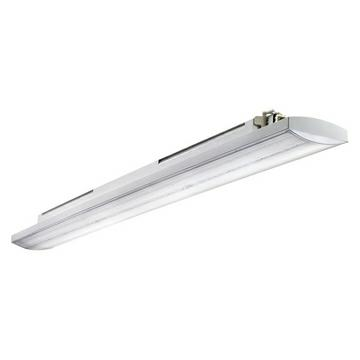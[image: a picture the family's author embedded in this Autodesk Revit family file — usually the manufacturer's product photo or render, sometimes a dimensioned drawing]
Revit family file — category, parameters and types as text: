
# Revit family: Lighting-Industrial-GEWISS-SMART[3]-WATERTIGHT-LED_TRASPARENT_800mm
name_source: partatom
category: Apparecchi per illuminazione
units: mm (PartAtom-declared; Revit-internal decimal feet)

## family parameters
Condiviso = No
Host = Superficie
Punto di calcolo locali = Sì
Quota connettore circolare = Usa diametro
Sorgente d'illuminazione = No
Taglio con vuoti quando caricato = No
Tipo di parte = Normale

## types (1)
- Lighting-Industrial-GEWISS-SMART[3]-WATERTIGHT-LED_TRASPARENT_800mm
    Application = Internal
    Body = Polycarbonate
    Catalogue = LIGHTING
    Catalogue Range = SMART [3]
    Classification: = -
    Color Rendering Index = CRI-80
    Colour = Grey (RAL 7035)
    Colour : = RAL7035 colored PC paste
    Colour temperature = 5700K
    Colour temperature: = 5700 K (CRI>80)
    Context = Lighting of warehouses, indoor parking and industrial production rooms
    Control System = Through wiring - DALI
    Control System : = DALI
    DIN 18032-3 certification = Not available
    Descrizione = SMART3 LED 800 2X18 TRASPAR.DALI 57K LP
    Device with reduced surface temperature = Yes
    Driver = Included
    Driver Box = Built-in
    Driver type = Constant Current Driver Led
    Efficiency (lm/W) = 126
    Efficiency class of integrated LEDs = A ÷ A++
    Electrocod = 2434
    Eletrical and lighting features = -
    External screw = -
    Failure rate apparecchio (35.000h, Tq=35° C) = <2,5%
    Failure rate apparecchio (50.000h, Tq=25° C) = <2,5%
    Fixing = Stainless steel support
    Ganci = GEWISS  - ALLUMINIO
    Gasket = CNC deposited sealant
    General information = -
    Glow Wire Test = 850°C
    Glow Wire Test : = 850 °C
    IDF = effa2bba-3d5b-4dc5-b978-3b29baa064f3
    IDT = ff6bcfd01228401f9ff1a7111276ab89
    IP degree = IP66/IP69
    IPEA = -
    Immagine tipo = GWS3118T.jpg
    Installationa and maintenance = -
    Insulation class = II
    LED Life Time (L90B50) = 50000H
    LED Life time (L80B50) = 100000H
    LED LifeTime (L80B20) = 85000H
    LED Maintenance = Not available
    Lamp- = LED
    Lampada = LED
    Length- = 800 mm
    Lifetime = L90B50 (Tq+25°C) = 50,000h - L80B10 (Tq+25°C) = 100,000h
    Locking Hook = -
    Lumen output (lm) = 3400
    Luminaire = LED fixture for general lighting
    Lunghezza Lampada = 800 mm  [stored 2.62467 ft]
    Materials = -
    Maximum surface exposed to the wind : = -
    Modello = GWS3218TLD57K
    Mouting and installation = Ceiling - Wallmounting - Suspension
    Nominal flux (lm) = 3500
    Operating temperature : = -25 +50 °C
    Operating temperature: = -30 +50 °C
    Optic = Microprismatic transparent
    Optic : = Integrated in the screen
    Optic Maintenance = Not available
    Optic and illuminating features = -
    Overvoltage protection = DM 1KV / CM 2KV
    Overvoltage resistance : = Common mode: 2KV; Differential mode: 1KV
    Photobiological Risk Class = RG0
    Produttore = GEWISS S.p.A.
    Prospetto di default = 1219 mm
    Rated frequency (Hz) = 50/60 Hz
    SEO = Luminaire
    Schermo- = Gewiss - Led Acceso
    Shield type = UV stabilised polycarbonate
    Shock resistance = IK08
    Stampa 1_100 = Sì
    Stampa 1_200 = No
    Standard Deviation Colour Matching = SDCM = 3
    Standard- = EN60598-1; IEC 62778; IEC62471
    Standards and approvals = -
    Stocking temperature = -25 +80 °C
    Struttura = GEWISS - SMART 3 - GRIGIO
    Supply voltage = 220 - 240 V
    System power = 27W
    Technical sheet = https://www.gewiss.com
    Tilt- = With fixing bracket
    Type of light source = LED - Not replaceable
    Typology = Dali - Feed through wiring
    URL = https://www.gewiss.com
    Unified Glare Rating = UGR - 25 (4H/4H)
    Unique digital code (Datamatrix) = Datamatrix
    Version file RFA = 20.11
    Voltage- = 220/240 V - 50/60 Hz - Dali
    Warranty = 5 years
    Weight (kg): = 1,5
    Wiring = With GW connect watertight connector
    Wiring : = Through wiring

note: [stored X ft] marks values corroborated as IEEE doubles in the binary element streams (Revit-internal decimal feet)
